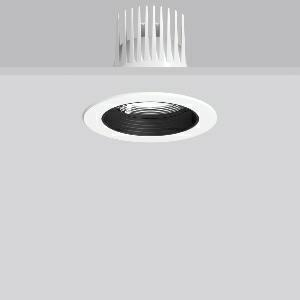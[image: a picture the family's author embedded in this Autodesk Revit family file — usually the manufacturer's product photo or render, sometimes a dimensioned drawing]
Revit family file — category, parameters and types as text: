
# Revit family: heledon_maxi_e_901761_002_2_5a92
name_source: partatom
category: Lighting Fixtures
units: mm (PartAtom-declared; Revit-internal decimal feet)

## family parameters
Cut with Voids When Loaded = No
Host = Face
Light Source = No
Part Type = Normal
Room Calculation Point = No
Round Connector Dimension = Use Diameter
Shared = No

## types (1)
- HELEDON maxi E (1 x LED Modul 927, 2550 lm, 2700)
    Apparent Load = 25 VA
    Approval mark = CE
    CIE Flux Codes = 96 100 100 100 100
    Color Rendering = 92
    Color Temperature = 2700
    Default Elevation = 1800 mm
    Description = Series: HELEDON maxi
Round recessed downlight. Housing: die-cast aluminium, powder-coated. Black plastic ring and recessed LED to prevent glare from the side. Optical assembly with lens made of plastic (polycarbonate) for the best homogeneous light distribution - can be changed without tools. Best colour rendering index Ra>90. Suitable for Recessed ceiling mounting. Installation without tools thanks to spring fastening system. Including separate LED converter with connecting cable 600 mm.High quality converter without flickering and stroboscopic effect. Through-wiring box (5 pole) available as accessory. The following accessories can be mounted without use of tools: interchangeable lenses, decorative glasses, honeycomb louvre, clear and frosted diffusers, white interchangeable plastic ring. 
Colour: traffic white, matt (RAL 9016)
Diameter: 162 mm
Height: 3 mm
Cut-out diameter: 152 mm
Recess height: 200 mm
Luminaire: recess height: 135 mm
Lamp: LED
Socket: without socket
Colour temperature: 2700K
Colour rendering index (CRI): 92
System power: 25 W
Rated luminous flux: 2550 lm
Luminous efficiency: 102 lm/W
Control gear: Regulated power supply
Protection class: II
Type of protection: IP 20
    Height = 0 mm  [stored 0 ft]
    Lamp = 1 x LED Modul 927
    Lamp Light Flux = 2550 lm
    Lamp count = 1
    Length = 162 mm
    Lifetime = 50000 h
    Luminous efficacy = 102 lm/W
    Manufacturer = RZB
    ModVariant = No
    Model = 901761.002.2
    Mounting Place = Ceiling
    Mounting Type = Recessed
    Number of Poles = 1
    OnlyDefault = Yes
    Power Factor = 1
    Product Name = HELEDON maxi E
    Product group = Recessed downlights
    ProductGroupID = 402
    Protection Class = Protection class II
    Protection Degree = IP 20
    RLX_Detail_Level = 1
    RLX_Emergency_Light_Flux = 0 lm
    RLX_Emergency_Type = 0
    RLX_Emergency_Type_DB = No
    RlxData = <blob elided: 119169 chars, md5=e4cb9dd8>
    Socket = socket
    Standby Power = 0 W
    System Light Flux = 2550 lm
    System Power = 25 W
    Type Comments = Product without accessories
    Type Image = 901663.002.jpg
    URL = http://relux.com
    VarID = ---
    Voltage = 230 V
    Voltage Range = 220-240 V
    Weight = 0.00 kg
    Width = 0 mm  [stored 0 ft]

note: [stored X ft] marks values corroborated as IEEE doubles in the binary element streams (Revit-internal decimal feet)

## geometry (parser evidence)
native form markers: Blend x4, Sweep x12
no freeform markers — native parametric forms only
